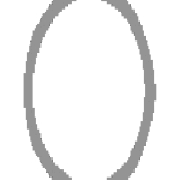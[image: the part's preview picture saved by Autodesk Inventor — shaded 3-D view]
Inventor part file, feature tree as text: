
AUTODESK INVENTOR PART (.ipt)
format: ipt  version: 2021 (Build 250183000, 183)  size: 108,544 bytes
history: native  units: in
note: dims shown in document units (in); Inventor stores cm internally (conversion verified against a paired STEP export)
features: other x4, sketch x3, plane x1
ambient origin geometry x8: Origin, YZ Plane, XZ Plane, XY Plane, X Axis, Y Axis, Z Axis, Center Point
bodies: Solid1 (feature_tree), Body (feature_tree)
feature tree (8):
  other  "Driven Length"
  other  "Frame Generator"
  other  "Start Plane"
  other  "End Plane"
  sketch  "Sketch"  dims[d2=38.7943in d4=-0.0in d5=38.7943in d6=0.12in d7=0.0in d8=90.0deg d9=38.7943in]
  sketch  "Sketch2"  dims[d0=1.0in]
  plane  "Work Plane3"
  sketch  "Sketch3"  dims[d1=0.065in]
